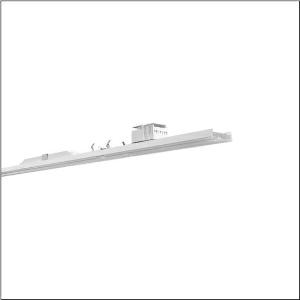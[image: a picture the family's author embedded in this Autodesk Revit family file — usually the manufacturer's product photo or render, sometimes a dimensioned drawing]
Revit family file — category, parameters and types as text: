
# Revit family: licross_r__21_recessed_mo_52tl19dnd75f_c119
name_source: partatom
category: Lighting Fixtures
units: mm (PartAtom-declared; Revit-internal decimal feet)

## family parameters
Cut with Voids When Loaded = No
Host = Face
Light Source = No
Part Type = Normal
Room Calculation Point = No
Round Connector Dimension = Use Diameter
Shared = No

## types (1)
- --- (1 x LED, 7630 lm, 61.1 W, 4000K)
    Apparent Load = 61 VA
    CIE Flux Codes = 55 90 98 100 100
    Color Rendering = 90
    Color Temperature = 4000K
    Default Elevation = 1800 mm
    Description = Licross® 21 Recessed MO, luminaire insert, of sheet steel, galvanised, coil coated, white, length: 1.500mm, width: 66mm, height: 67mm, LED rated luminous flux: 7.630lm, light colour: 940, control gear: DALI 2, control gear: ECG DALI, with plug, 5-pole, with phase selection, mains connection: 220..240V, AC, 50/60Hz, rated input power: 61W, halogen-free wiring, primary light control with lens, of plastic, primary optical cover: cover, of PMMA, light emission: direct distribution, primary light characteristic: double asymmetric, protection rating (complete): IP40, insulation class (complete): insulation class I (protective earthing), certification: CE, ENEC, VDE, UKCA, protection symbol: D if used in an environment without relevant dust loads with corresponding accessories, impact resistance: IK06, permissible ambient temperature for indoor applications: -25..+35°C, corresponds to IFS (International Featured Standards) requirements for safety and quality in the food industry, reducing of maximum allowable ambient temperature of 5°C with ceiling mounting, LABS conformity tested according to VDMA 24364:2018-05, packaging unit: 1 piece
    Height = 58 mm
    Lamp = 1 x LED
    Lamp Light Flux = 7630 lm
    Lamp Power = 61.1 W
    Lamp count = 1
    Length = 1500 mm
    Luminous efficacy = 125 lm/W
    Manufacturer = Siteco
    ModVariant = No
    Model = 52TL19DND75F
    Mounting Place = Ceiling
    Mounting Type = Pendant
    Number of Poles = 1
    OnlyDefault = Yes
    Power Factor = 1
    Product Name = Licross® 21 Recessed MO
    Product group = luminaire insert
    ProductGroupID = 901
    Protection Class = Protection class I
    Protection Degree = IP 40
    RLX_Detail_Level = 1
    RLX_Emergency_Light_Flux = 0 lm
    RLX_Emergency_Type = 0
    RLX_Emergency_Type_DB = No
    RlxData = <blob elided: 22633 chars, md5=38fa18f1>
    Socket = socket
    Standby Power = 0 W
    System Light Flux = 7630 lm
    System Power = 61 W
    Type Comments = factory setting: luminous flux: 100 % | dim-lin: 254 | 405 mA
    Type Image = l_1296935.jpg
    URL = http://relux.com
    VarID = @adj_136317
    Voltage = 0 V
    Weight = 0.00 kg
    Width = 66 mm

## geometry (parser evidence)
native form markers: Blend x4, Sweep x9
no freeform markers — native parametric forms only
